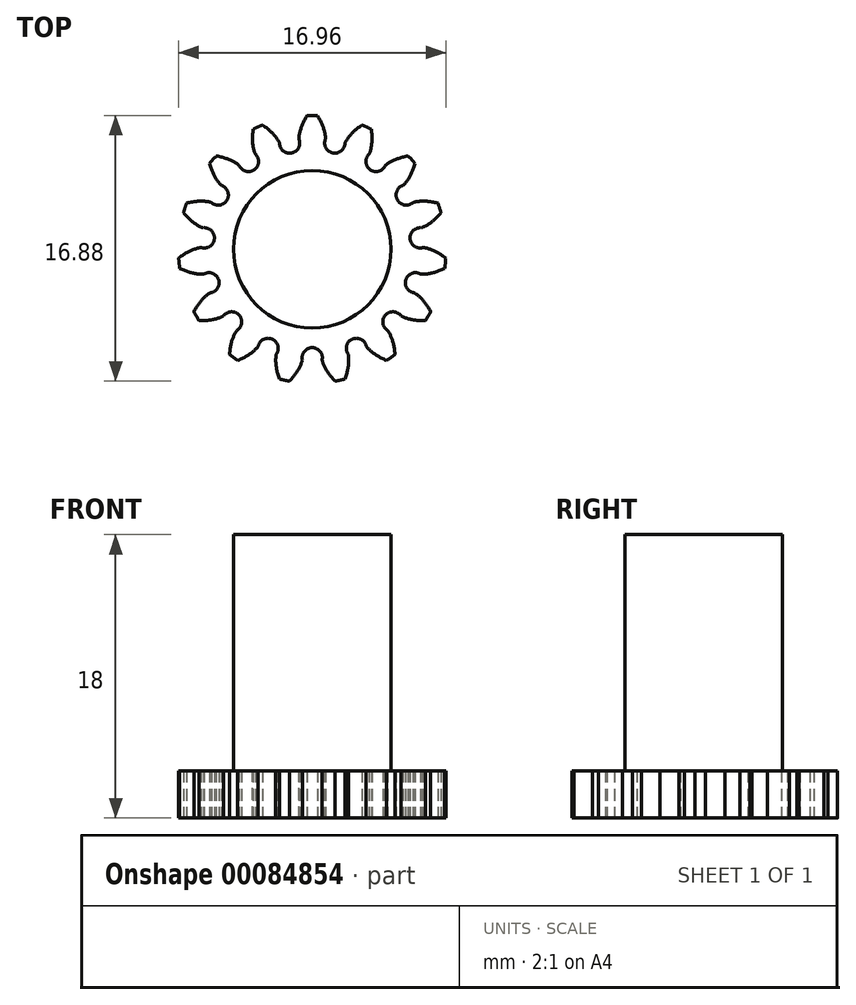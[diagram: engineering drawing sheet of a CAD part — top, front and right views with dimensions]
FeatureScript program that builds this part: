
annotation { "Feature Type Name" : "Feature", "Feature Type Description" : "" }
export const myFeature = defineFeature(function(context is Context, id is Id, definition is map)
    precondition{}
    {
        {
            assignVariable(context, id + "F0", {"name" : "Z", "anyValue" : 15});
        }
        {
            assignVariable(context, id + "F1", {"name" : "e", "anyValue" : 3});
        }
        {
            var Q0;
            Q0=qCreatedBy(makeId("Top.planeOp"),FACE);
            var sketch = newSketch(context, id + "F2", { "sketchPlane" : qUnion([Q0])});
            skCircle(sketch, "E0", {"center": v(0, 0) * mm, "radius": 7.5 * mm, "construction": true});
            skCircle(sketch, "E1", {"center": v(0, 0) * mm, "radius": 8.5 * mm, "construction": true});
            skLineSegment(sketch, "E2", {"start": v(-8.95, 7.5) * mm, "end": v(8.95, 7.5) * mm, "construction": true});
            skLineSegment(sketch, "E3", {"start": v(0, 0) * mm, "end": v(0, 7.5) * mm, "construction": true});
            skLineSegment(sketch, "E4", {"start": v(-2.41, 6.62) * mm, "end": v(0, 7.5) * mm, "construction": true});
            skLineSegment(sketch, "E5", {"start": v(0, 0) * mm, "end": v(-2.41, 6.62) * mm, "construction": true});
            skCircle(sketch, "E6", {"center": v(0, 0) * mm, "radius": 7.05 * mm, "construction": true});
            skLineSegment(sketch, "E7", {"start": v(-0.84, 7) * mm, "end": v(0.34, 7.04) * mm, "construction": true});
            skLineSegment(sketch, "E8", {"start": v(0.34, 7.04) * mm, "end": v(1.52, 6.88) * mm, "construction": true});
            skLineSegment(sketch, "E9", {"start": v(1.52, 6.88) * mm, "end": v(2.66, 6.53) * mm, "construction": true});
            skLineSegment(sketch, "E10", {"start": v(2.66, 6.53) * mm, "end": v(3.71, 5.99) * mm, "construction": true});
            skLineSegment(sketch, "E11", {"start": v(0.34, 7.04) * mm, "end": v(-0.84, 7.1) * mm, "construction": true});
            skLineSegment(sketch, "E12", {"start": v(2.66, 6.53) * mm, "end": v(1.55, 6.98) * mm, "construction": true});
            skLineSegment(sketch, "E13", {"start": v(1.55, 6.98) * mm, "end": v(0.45, 7.42) * mm, "construction": true});
            skLineSegment(sketch, "E14", {"start": v(0.45, 7.42) * mm, "end": v(-0.65, 7.87) * mm, "construction": true});
            skLineSegment(sketch, "E15", {"start": v(3.71, 5.99) * mm, "end": v(2.7, 6.62) * mm, "construction": true});
            skLineSegment(sketch, "E16", {"start": v(2.7, 6.62) * mm, "end": v(1.7, 7.24) * mm, "construction": true});
            skLineSegment(sketch, "E17", {"start": v(1.7, 7.24) * mm, "end": v(0.69, 7.87) * mm, "construction": true});
            skLineSegment(sketch, "E18", {"start": v(0.69, 7.87) * mm, "end": v(-0.32, 8.5) * mm, "construction": true});
            skLineSegment(sketch, "E19", {"start": v(1.52, 6.88) * mm, "end": v(0.36, 7.14) * mm, "construction": true});
            skLineSegment(sketch, "E20", {"start": v(0.36, 7.14) * mm, "end": v(-0.8, 7.4) * mm, "construction": true});
            skLineSegment(sketch, "E21", {"start": v(0, 0) * mm, "end": v(-0.84, 7) * mm, "construction": true});
            skFitSpline(sketch, "E22", {"points": [v(-0.84, 7) * mm, v(-0.84, 7.1) * mm, v(-0.8, 7.4) * mm, v(-0.65, 7.87) * mm, v(-0.32, 8.5) * mm], "startDerivative": vector(-0.1, 0.8) * mm, "endDerivative": vector(1.32, 2.13) * mm});
            skLineSegment(sketch, "E23", {"start": v(-0.32, 8.5) * mm, "end": v(-1.3, 6.93) * mm, "construction": true});
            skFitSpline(sketch, "E24.MirrorCS", {"points": [v(0.84, 7) * mm, v(0.84, 7.1) * mm, v(0.8, 7.4) * mm, v(0.65, 7.87) * mm, v(0.32, 8.5) * mm], "startDerivative": vector(0.1, 0.8) * mm, "endDerivative": vector(-1.32, 2.13) * mm});
            skArc(sketch, "E25", {"start": v(0.32, 8.5) * mm, "mid": v(0, 8.5) * mm, "end": v(-0.32, 8.5) * mm});
            skCircle(sketch, "E26", {"center": v(0, 0) * mm, "radius": 6.25 * mm, "construction": true});
            skLineSegment(sketch, "E27", {"start": v(0, 0) * mm, "end": v(-1.3, 6.11) * mm});
            skArc(sketch, "E28", {"start": v(-1.3, 6.11) * mm, "mid": v(-0.86, 6.45) * mm, "end": v(-0.84, 7) * mm});
            skArc(sketch, "E29.MirrorCS", {"start": v(1.3, 6.11) * mm, "mid": v(0.86, 6.45) * mm, "end": v(0.84, 7) * mm});
            skLineSegment(sketch, "E30.MirrorCS", {"start": v(0, 0) * mm, "end": v(1.3, 6.11) * mm});
            skArc(sketch, "E31", {"start": v(0.78, 7.46) * mm, "mid": v(0, 7.5) * mm, "end": v(-0.78, 7.46) * mm, "construction": true});
            skSolve(sketch);
        }
        {
            var Q0;
            Q0=makeQuery(id+"F2.imprint","IMPRINT",FACE,{"disambiguationData":[TD([[makeQuery(id+"F2.imprint","IMPRINT",EDGE,{"derivedFrom":sQuery(id+"F2.wireOp",EDGE,"E22")}),-1.0]])]});
            extrude(context, id + "F3", {"entities" : qUnion([Q0]), "endBound" : BoundingType.SYMMETRIC, "depth" : (getVariable(context, 'e')) * mm});
        }
        {
            var Q0;
            Q0=makeQuery(id+"F3.opExtrude","SWEPT_BODY",BODY,{"disambiguationData":[OSD([sQuery(id+"F2.wireOp",EDGE,"E22"),sQuery(id+"F2.wireOp",EDGE,"E24.MirrorCS"),sQuery(id+"F2.wireOp",EDGE,"E25"),sQuery(id+"F2.wireOp",EDGE,"E27"),sQuery(id+"F2.wireOp",EDGE,"E28"),sQuery(id+"F2.wireOp",EDGE,"E29.MirrorCS"),sQuery(id+"F2.wireOp",EDGE,"E30.MirrorCS")])]});
            var Q1;
            Q1=makeQuery(id+"F3.opExtrude","SWEPT_EDGE",EDGE,{"disambiguationData":[OSD([sQuery(id+"F2.wireOp",EDGE,"E27"),sQuery(id+"F2.wireOp",EDGE,"E30.MirrorCS")])]});
            circularPattern(context, id + "F4", {"operationType" : NewBodyOperationType.ADD, "entities" : qUnion([Q0]), "axis" : qUnion([Q1]), "angle" : 360 * degree, "instanceCount" : getVariable(context, 'Z'), "equalSpace" : true});
        }
        {
            var Q0;
            {var subQ0=makeQuery(id+"F3.opExtrude","CAP_FACE",FACE,{"disambiguationData":[OSD([sQuery(id+"F2.wireOp",EDGE,"E22"),sQuery(id+"F2.wireOp",EDGE,"E24.MirrorCS"),sQuery(id+"F2.wireOp",EDGE,"E25"),sQuery(id+"F2.wireOp",EDGE,"E27"),sQuery(id+"F2.wireOp",EDGE,"E28"),sQuery(id+"F2.wireOp",EDGE,"E29.MirrorCS"),sQuery(id+"F2.wireOp",EDGE,"E30.MirrorCS")])],"isStart":false});Q0=makeQuery(id+"F4.boolean.opBoolean","MERGE",FACE,{"derivedFrom":[subQ0,makeQuery(id+"F4.opPattern","COPY",FACE,{"derivedFrom":subQ0,"instanceName":"1"}),makeQuery(id+"F4.opPattern","COPY",FACE,{"derivedFrom":subQ0,"instanceName":"2"}),makeQuery(id+"F4.opPattern","COPY",FACE,{"derivedFrom":subQ0,"instanceName":"3"}),makeQuery(id+"F4.opPattern","COPY",FACE,{"derivedFrom":subQ0,"instanceName":"4"}),makeQuery(id+"F4.opPattern","COPY",FACE,{"derivedFrom":subQ0,"instanceName":"5"}),makeQuery(id+"F4.opPattern","COPY",FACE,{"derivedFrom":subQ0,"instanceName":"6"}),makeQuery(id+"F4.opPattern","COPY",FACE,{"derivedFrom":subQ0,"instanceName":"7"}),makeQuery(id+"F4.opPattern","COPY",FACE,{"derivedFrom":subQ0,"instanceName":"8"}),makeQuery(id+"F4.opPattern","COPY",FACE,{"derivedFrom":subQ0,"instanceName":"9"}),makeQuery(id+"F4.opPattern","COPY",FACE,{"derivedFrom":subQ0,"instanceName":"10"}),makeQuery(id+"F4.opPattern","COPY",FACE,{"derivedFrom":subQ0,"instanceName":"11"}),makeQuery(id+"F4.opPattern","COPY",FACE,{"derivedFrom":subQ0,"instanceName":"12"}),makeQuery(id+"F4.opPattern","COPY",FACE,{"derivedFrom":subQ0,"instanceName":"13"}),makeQuery(id+"F4.opPattern","COPY",FACE,{"derivedFrom":subQ0,"instanceName":"14"}),makeQuery(id+"F4.opPattern","COPY",FACE,{"derivedFrom":subQ0,"instanceName":"15"}),makeQuery(id+"F4.opPattern","COPY",FACE,{"derivedFrom":subQ0,"instanceName":"16"}),makeQuery(id+"F4.opPattern","COPY",FACE,{"derivedFrom":subQ0,"instanceName":"17"}),makeQuery(id+"F4.opPattern","COPY",FACE,{"derivedFrom":subQ0,"instanceName":"18"}),makeQuery(id+"F4.opPattern","COPY",FACE,{"derivedFrom":subQ0,"instanceName":"19"}),makeQuery(id+"F4.opPattern","COPY",FACE,{"derivedFrom":subQ0,"instanceName":"20"}),makeQuery(id+"F4.opPattern","COPY",FACE,{"derivedFrom":subQ0,"instanceName":"21"}),makeQuery(id+"F4.opPattern","COPY",FACE,{"derivedFrom":subQ0,"instanceName":"22"}),makeQuery(id+"F4.opPattern","COPY",FACE,{"derivedFrom":subQ0,"instanceName":"23"}),makeQuery(id+"F4.opPattern","COPY",FACE,{"derivedFrom":subQ0,"instanceName":"24"}),makeQuery(id+"F4.opPattern","COPY",FACE,{"derivedFrom":subQ0,"instanceName":"25"})]});}
            var sketch = newSketch(context, id + "F5", { "sketchPlane" : qUnion([Q0])});
            skCircle(sketch, "E32", {"center": v(0, 0) * mm, "radius": 5 * mm});
            skSolve(sketch);
        }
        {
            var Q0;
            Q0 = qSketchRegion(id + "F5", true);
            extrude(context, id + "F6", {"entities" : qUnion([Q0]), "operationType" : NewBodyOperationType.ADD, "depth" : 15 * mm});
        }
    });
